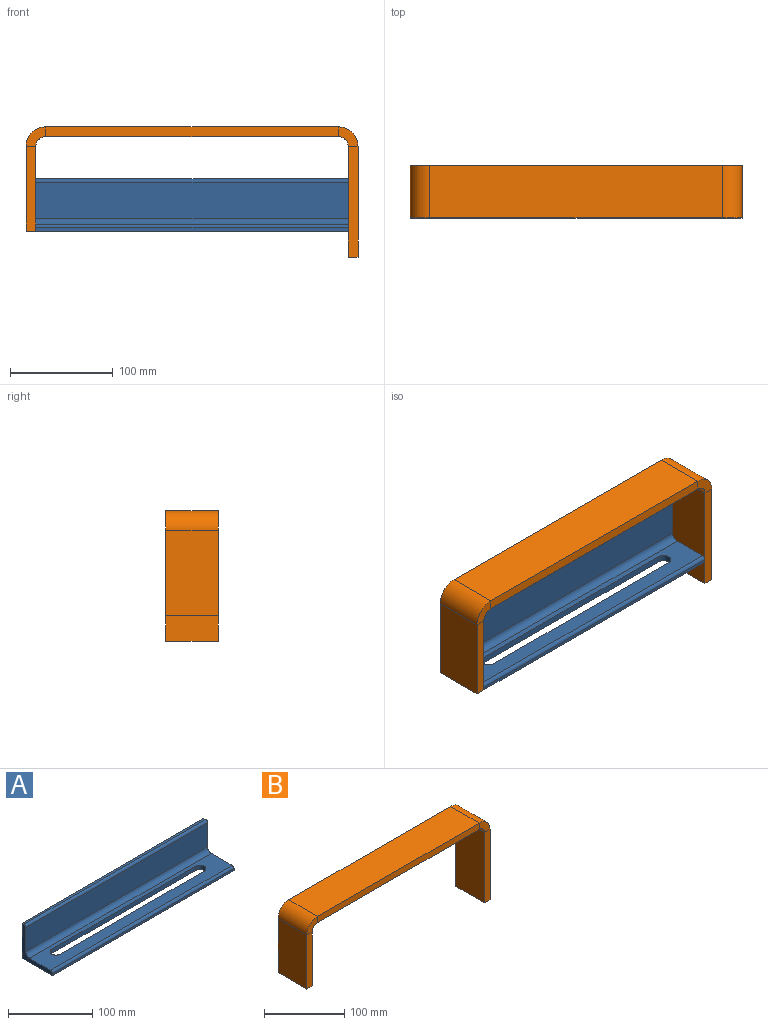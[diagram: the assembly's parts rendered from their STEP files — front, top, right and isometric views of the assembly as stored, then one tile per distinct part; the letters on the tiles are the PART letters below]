
ASSEMBLY  parts=2 mates=1
PART A: 15 faces, bbox 304.8x50.8x50.8 mm
  f0: plane 50.8x50.8mm, normal (1,0,0), area 609.2mm2, adj f2,f3,f4,f5,f6,f7,f8,f9
  f1: plane 50.8x50.8mm, normal (-1,0,0), area 609.2mm2, adj f2,f3,f4,f5,f6,f7,f8,f9
  f2: cylinder r=3.17mm len=304.8mm, axis (-1,0,0), area 1520.1mm2, adj f0,f1,f3,f10
  f3: plane 304.8x34.93mm, normal (0,0,1), area 7037.2mm2, adj f0,f1,f2,f4,f11,f12,f13,f14
  f4: cylinder r=6.35mm len=304.8mm, axis (-1,0,0), area 3040.3mm2, adj f0,f1,f3,f5
  f5: plane 304.8x34.93mm, normal (0,-1,0), area 10645.1mm2, adj f0,f1,f4,f6
  f6: cylinder r=3.17mm len=304.8mm, axis (-1,0,0), area 1520.1mm2, adj f0,f1,f5,f7
  f7: plane 304.8x3.18mm, normal (0,0,1), area 967.7mm2, adj f0,f1,f6,f8
  f8: plane 304.8x50.8mm, normal (0,1,0), area 15483.8mm2, adj f0,f1,f7,f9
  f9: plane 304.8x50.8mm, normal (0,0,-1), area 11875.9mm2, adj f0,f1,f8,f10,f11,f12,f13,f14
  f10: plane 304.8x3.18mm, normal (0,-1,0), area 967.7mm2, adj f0,f1,f2,f9
  f11: plane 241.3x6.35mm, normal (0,1,0), area 1532.3mm2, adj f3,f9,f12,f14
  f12: cylinder r=7.14mm len=14.29mm, axis (0,0,-1), area 142.5mm2, adj f3,f9,f11,f13
  f13: plane 241.3x6.35mm, normal (0,-1,0), area 1532.3mm2, adj f3,f9,f12,f14
  f14: cylinder r=7.14mm len=14.29mm, axis (0,0,-1), area 142.5mm2, adj f3,f9,f11,f13
PART B: 22 faces, bbox 323.9x50.8x127 mm
  f0: plane 285.75x9.53mm, normal (0,1,0), area 2721.8mm2, adj f2,f3,f10,f19
  f1: plane 285.75x9.53mm, normal (0,-1,0), area 2721.8mm2, adj f2,f3,f9,f18
  f2: plane 285.75x50.8mm, normal (0,0,1), area 14516.1mm2, adj f0,f1,f11,f20
  f3: plane 285.75x50.8mm, normal (0,0,-1), area 14516.1mm2, adj f0,f1,f12,f21
  f4: plane 50.8x9.53mm, normal (0,0,-1), area 483.9mm2, adj f5,f6,f7,f8
  f5: plane 107.95x9.53mm, normal (0,1,0), area 1028.2mm2, adj f4,f7,f8,f10
  f6: plane 107.95x9.53mm, normal (0,-1,0), area 1028.2mm2, adj f4,f7,f8,f9
  f7: plane 107.95x50.8mm, normal (1,0,0), area 5483.9mm2, adj f4,f5,f6,f11
  f8: plane 107.95x50.8mm, normal (-1,0,0), area 5483.9mm2, adj f4,f5,f6,f12
  f9: plane 19.05x19.05mm, normal (0,-1,0), area 213.8mm2, adj f1,f6,f11,f12
  f10: plane 19.05x19.05mm, normal (0,1,0), area 213.8mm2, adj f0,f5,f11,f12
  f11: cylinder r=19.05mm len=50.8mm, axis (0,-1,0), area 1520.1mm2, adj f2,f7,f9,f10
  f12: cylinder r=9.53mm len=50.8mm, axis (0,-1,0), area 760.1mm2, adj f3,f8,f9,f10
  f13: plane 50.8x9.53mm, normal (0,0,-1), area 483.9mm2, adj f14,f15,f16,f17
  f14: plane 82.55x9.53mm, normal (0,-1,0), area 786.3mm2, adj f13,f16,f17,f18
  f15: plane 82.55x9.53mm, normal (0,1,0), area 786.3mm2, adj f13,f16,f17,f19
  f16: plane 82.55x50.8mm, normal (-1,0,0), area 4193.5mm2, adj f13,f14,f15,f20
  f17: plane 82.55x50.8mm, normal (1,0,0), area 4193.5mm2, adj f13,f14,f15,f21
  f18: plane 19.05x19.05mm, normal (0,-1,0), area 213.8mm2, adj f1,f14,f20,f21
  f19: plane 19.05x19.05mm, normal (0,1,0), area 213.8mm2, adj f0,f15,f20,f21
  f20: cylinder r=19.05mm len=50.8mm, axis (0,-1,0), area 1520.1mm2, adj f2,f16,f18,f19
  f21: cylinder r=9.53mm len=50.8mm, axis (0,-1,0), area 760.1mm2, adj f3,f17,f18,f19
PLACE A t=(54.01,7.78,33.38)mm
PLACE B t=(54.01,7.78,125.46)mm
MATE fastened B.f17 <-> A.f1  axis (1,0,0) through (-250.79,7.78,33.38)mm
